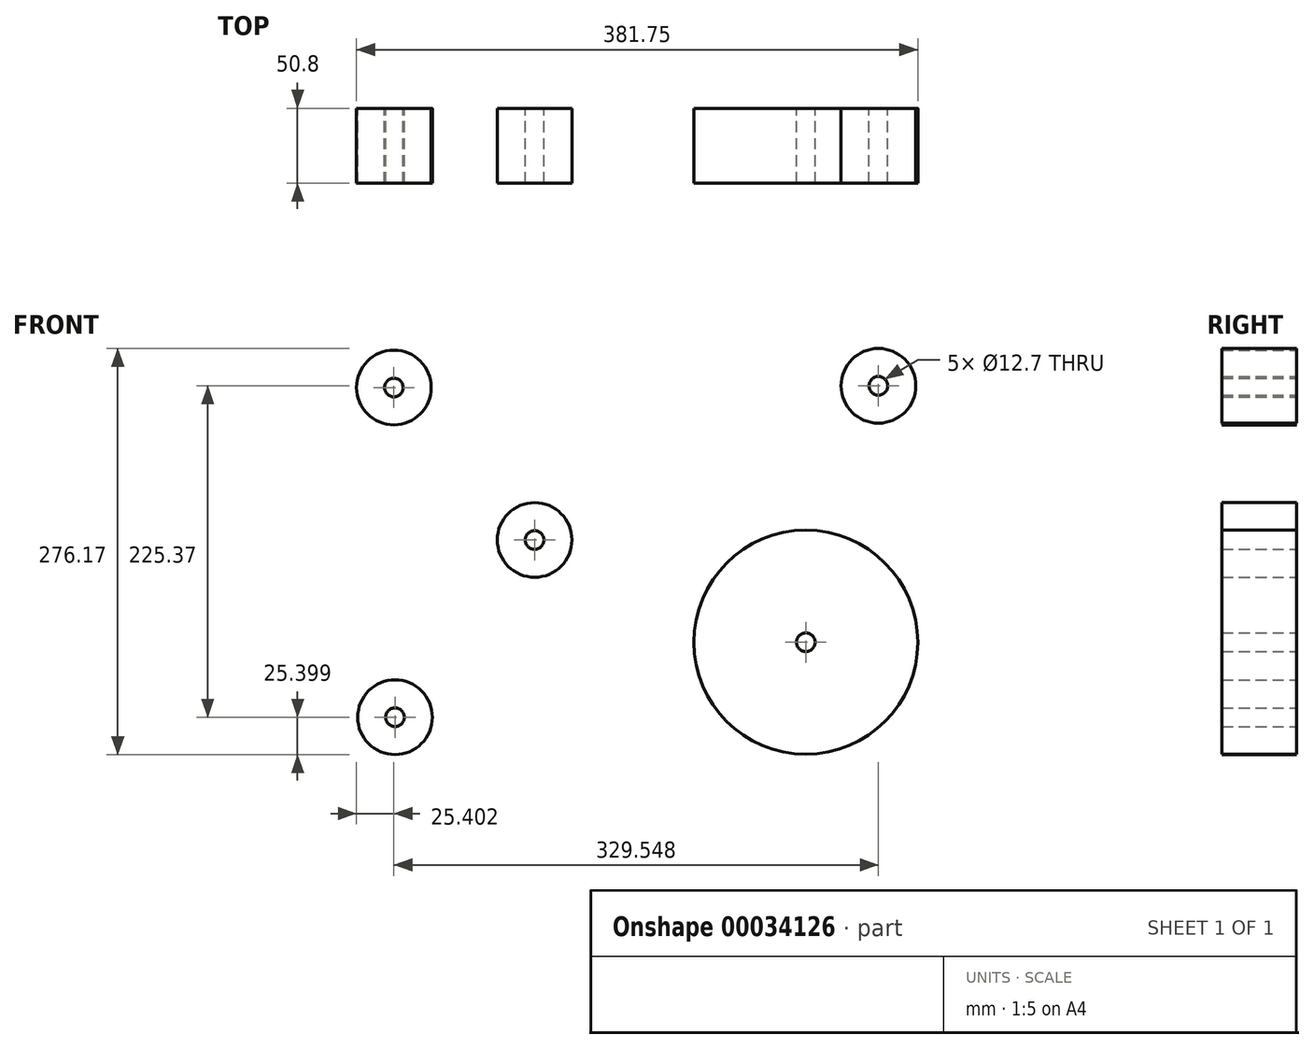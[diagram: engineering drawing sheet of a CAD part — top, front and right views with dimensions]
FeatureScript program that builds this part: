
annotation { "Feature Type Name" : "Feature", "Feature Type Description" : "" }
export const myFeature = defineFeature(function(context is Context, id is Id, definition is map)
    precondition{}
    {
        {
            var Q0;
            Q0=qCreatedBy(makeId("Front.planeOp"),FACE);
            var sketch = newSketch(context, id + "F0", { "sketchPlane" : qUnion([Q0])});
            skCircle(sketch, "E0", {"center": v(-316.33, 152.49) * mm, "radius": 25.4 * mm});
            skCircle(sketch, "E1", {"center": v(13.22, 153.65) * mm, "radius": 25.4 * mm});
            skCircle(sketch, "E2", {"center": v(-315.53, -71.72) * mm, "radius": 25.4 * mm});
            skCircle(sketch, "E3", {"center": v(-220.59, 48.85) * mm, "radius": 25.4 * mm});
            skSolve(sketch);
        }
        {
            var Q0;
            Q0=qCreatedBy(makeId("Front.planeOp"),FACE);
            var sketch = newSketch(context, id + "F1", { "sketchPlane" : qUnion([Q0])});
            skCircle(sketch, "E4", {"center": v(-36.18, -20.72) * mm, "radius": 76.2 * mm});
            skSolve(sketch);
        }
        {
            var Q0;
            Q0=makeQuery(id+"F0.imprint","IMPRINT",FACE,{"disambiguationData":[TD([[makeQuery(id+"F0.imprint","IMPRINT",EDGE,{"derivedFrom":sQuery(id+"F0.wireOp",EDGE,"E0")}),1.0]])]});
            var Q1;
            Q1=makeQuery(id+"F0.imprint","IMPRINT",FACE,{"disambiguationData":[TD([[makeQuery(id+"F0.imprint","IMPRINT",EDGE,{"derivedFrom":sQuery(id+"F0.wireOp",EDGE,"E2")}),1.0]])]});
            var Q2;
            Q2=makeQuery(id+"F0.imprint","IMPRINT",FACE,{"disambiguationData":[TD([[makeQuery(id+"F0.imprint","IMPRINT",EDGE,{"derivedFrom":sQuery(id+"F0.wireOp",EDGE,"E1")}),1.0]])]});
            var Q3;
            Q3=makeQuery(id+"F1.imprint","IMPRINT",FACE,{"disambiguationData":[TD([[makeQuery(id+"F1.imprint","IMPRINT",EDGE,{"derivedFrom":sQuery(id+"F1.wireOp",EDGE,"E4")}),1.0]])]});
            extrude(context, id + "F2", {"entities" : qUnion([Q0, Q1, Q2, Q3]), "depth" : 50.8 * mm});
        }
        {
            var Q0;
            Q0=qCreatedBy(makeId("Front.planeOp"),FACE);
            var sketch = newSketch(context, id + "F3", { "sketchPlane" : qUnion([Q0])});
            skFitSpline(sketch, "E5", {"points": [v(42.26, -24.36) * mm, v(42.26, 149.81) * mm, v(42.86, 158.3) * mm, v(32.4, 176.32) * mm, v(2.76, 180.97) * mm, v(-64.85, 163.75) * mm, v(-141.92, 163.75) * mm, v(-253.83, 162.44) * mm, v(-304.12, 180.38) * mm, v(-332.6, 175.74) * mm, v(-343.72, 160.94) * mm, v(-343.96, 160.7) * mm, v(-346.58, 142.98) * mm, v(-346.57, 142.85) * mm, v(-340.04, 121.07) * mm, v(-210.56, 75.15) * mm, v(-193.7, 54.84) * mm, v(-208.27, 22.88) * mm, v(-323.3, -39.31) * mm, v(-342.65, -55.27) * mm, v(-346.13, -84.88) * mm, v(-310.43, -103.17) * mm, v(-119.72, -102.3) * mm, v(6.56, -94.46) * mm, v(30.94, -78.35) * mm, v(41.39, -46.56) * mm, v(42.26, -24.36) * mm]});
            skSolve(sketch);
        }
        {
            var Q0;
            Q0=sQuery(id+"F3.wireOp",EDGE,"E5");
            extrude(context, id + "F4", {"bodyType" : ToolBodyType.SURFACE, "surfaceEntities" : qUnion([Q0]), "depth" : 50.8 * mm});
        }
        {
            var Q0;
            Q0=makeQuery(id+"F0.imprint","IMPRINT",FACE,{"disambiguationData":[TD([[makeQuery(id+"F0.imprint","IMPRINT",EDGE,{"derivedFrom":sQuery(id+"F0.wireOp",EDGE,"E3")}),1.0]])]});
            extrude(context, id + "F5", {"entities" : qUnion([Q0]), "depth" : 50.8 * mm});
        }
        {
            var Q0;
            Q0=sQuery(id+"F0.wireOp",VERTEX,"E2.center");
            var Q1;
            Q1=sQuery(id+"F0.wireOp",VERTEX,"E0.center");
            var Q2;
            Q2=sQuery(id+"F0.wireOp",VERTEX,"E1.center");
            var Q3;
            Q3=sQuery(id+"F1.wireOp",VERTEX,"E4.center");
            var Q4;
            Q4=sQuery(id+"F0.wireOp",VERTEX,"E3.center");
            var Q5;
            Q5=makeQuery(id+"F2.opExtrude","SWEPT_BODY",BODY,{"disambiguationData":[OSD([sQuery(id+"F0.wireOp",EDGE,"E2")])]});
            var Q6;
            Q6=makeQuery(id+"F2.opExtrude","SWEPT_BODY",BODY,{"disambiguationData":[OSD([sQuery(id+"F0.wireOp",EDGE,"E0")])]});
            var Q7;
            Q7=makeQuery(id+"F2.opExtrude","SWEPT_BODY",BODY,{"disambiguationData":[OSD([sQuery(id+"F0.wireOp",EDGE,"E1")])]});
            var Q8;
            Q8=makeQuery(id+"F2.opExtrude","SWEPT_BODY",BODY,{"disambiguationData":[OSD([sQuery(id+"F1.wireOp",EDGE,"E4")])]});
            hole(context, id + "F6", {"style" : HoleStyle.SIMPLE, "holeDiameter" : 12.7 * mm, "endStyle" : HoleEndStyle.THROUGH, "oppositeDirection" : true, "locations" : qUnion([Q0, Q1, Q2, Q3, Q4]), "scope" : qUnion([Q5, Q6, Q7, Q8])});
        }
        {
            var Q0;
            Q0=sQuery(id+"F0.wireOp",VERTEX,"E3.center");
            var Q1;
            Q1=makeQuery(id+"F5.opExtrude","SWEPT_BODY",BODY,{"disambiguationData":[OSD([sQuery(id+"F0.wireOp",EDGE,"E3")])]});
            hole(context, id + "F7", {"style" : HoleStyle.SIMPLE, "holeDiameter" : 12.7 * mm, "endStyle" : HoleEndStyle.THROUGH, "oppositeDirection" : true, "locations" : qUnion([Q0]), "scope" : qUnion([Q1])});
        }
    });
